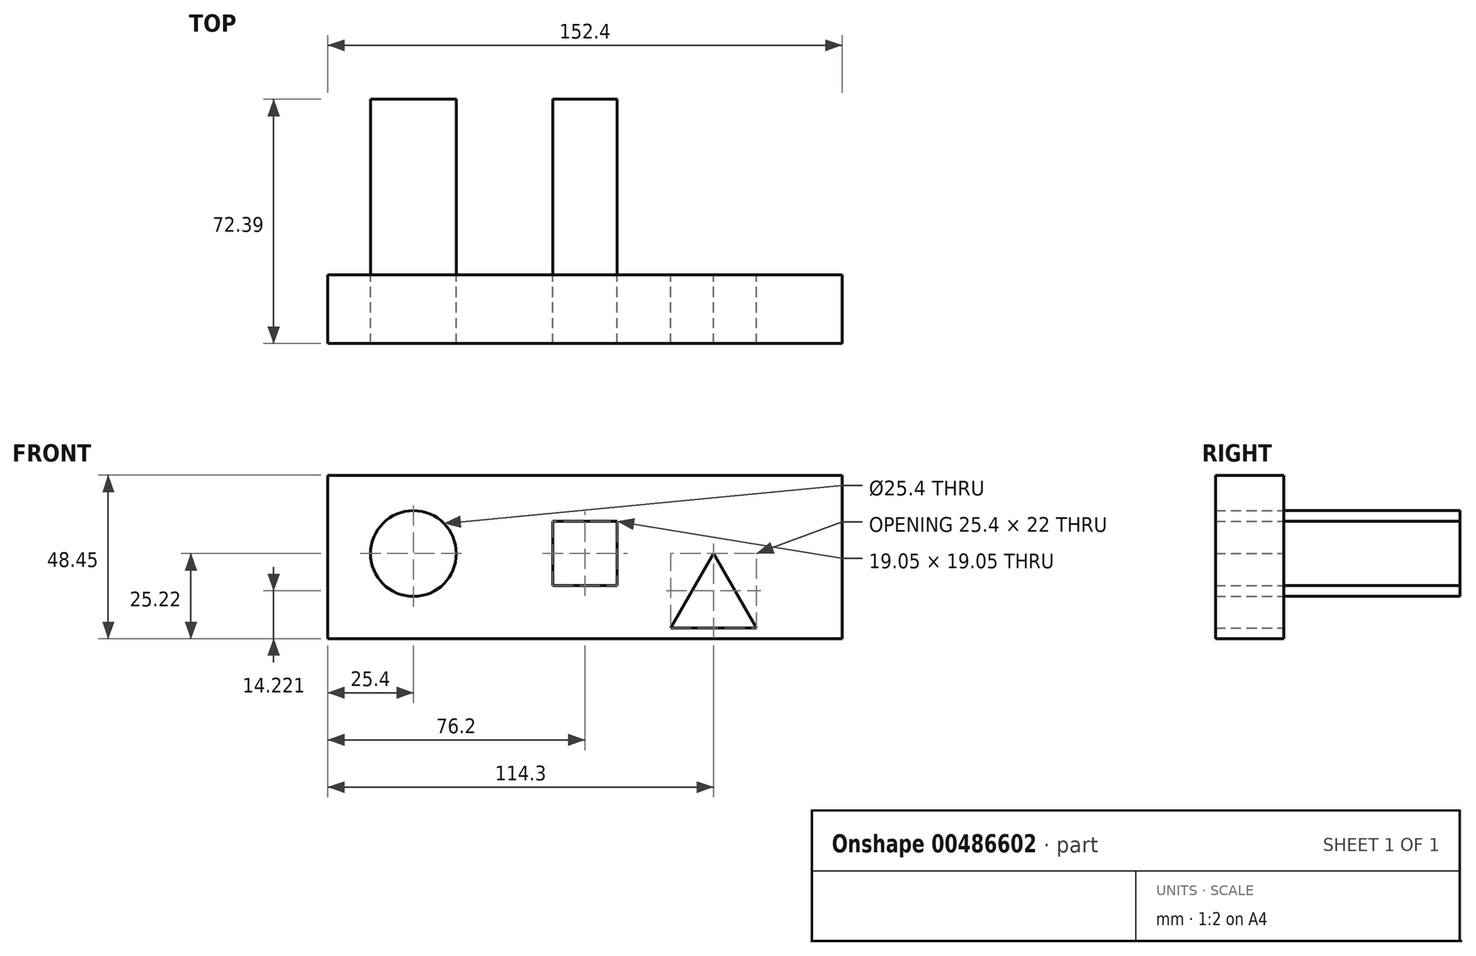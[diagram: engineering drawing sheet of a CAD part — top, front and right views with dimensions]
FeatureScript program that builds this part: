
annotation { "Feature Type Name" : "Feature", "Feature Type Description" : "" }
export const myFeature = defineFeature(function(context is Context, id is Id, definition is map)
    precondition{}
    {
        {
            var Q0;
            Q0=qCreatedBy(makeId("Front.planeOp"),FACE);
            var sketch = newSketch(context, id + "F0", { "sketchPlane" : qUnion([Q0])});
            skPoint(sketch, "E0.middle", {"position": v(0, 0) * mm});
            skLineSegment(sketch, "E1", {"start": v(0, 0) * mm, "end": v(6.35, 0) * mm});
            skLineSegment(sketch, "E2", {"start": v(6.35, 0) * mm, "end": v(-6.35, -22) * mm});
            skLineSegment(sketch, "E3", {"start": v(6.35, 0) * mm, "end": v(19.05, -22) * mm});
            skLineSegment(sketch, "E4", {"start": v(19.05, -22) * mm, "end": v(-6.35, -22) * mm});
            skLineSegment(sketch, "E5", {"start": v(-31.75, 0) * mm, "end": v(0, 0) * mm});
            skLineSegment(sketch, "E6.bottom", {"start": v(-41.27, 9.53) * mm, "end": v(-22.22, 9.52) * mm});
            skLineSegment(sketch, "E6.top", {"start": v(-41.27, -9.53) * mm, "end": v(-22.23, -9.53) * mm});
            skLineSegment(sketch, "E6.left", {"start": v(-41.27, 9.53) * mm, "end": v(-41.28, -9.53) * mm});
            skLineSegment(sketch, "E6.right", {"start": v(-22.22, 9.52) * mm, "end": v(-22.23, -9.53) * mm});
            skPoint(sketch, "E6.middle", {"position": v(-31.75, 0) * mm});
            skLineSegment(sketch, "E7", {"start": v(-31.75, 0) * mm, "end": v(-82.55, 0) * mm});
            skCircle(sketch, "E8", {"center": v(-82.55, 0) * mm, "radius": 12.7 * mm});
            skLineSegment(sketch, "E9", {"start": v(0, 0) * mm, "end": v(44.45, 0) * mm});
            skPoint(sketch, "E9.endSnap0", {"position": v(3.18, 0) * mm});
            skLineSegment(sketch, "E10", {"start": v(44.45, 0) * mm, "end": v(44.45, -25.22) * mm});
            skLineSegment(sketch, "E11.bottom", {"start": v(44.45, -25.22) * mm, "end": v(-107.95, -25.22) * mm});
            skLineSegment(sketch, "E11.top", {"start": v(44.45, 23.23) * mm, "end": v(-107.95, 23.23) * mm});
            skLineSegment(sketch, "E11.left", {"start": v(44.45, -25.22) * mm, "end": v(44.45, 23.23) * mm});
            skLineSegment(sketch, "E11.right", {"start": v(-107.95, -25.22) * mm, "end": v(-107.95, 23.23) * mm});
            skSolve(sketch);
        }
        {
            var Q0;
            Q0 = qSketchRegion(id + "F0", true);
            extrude(context, id + "F1", {"entities" : qUnion([Q0]), "depth" : 20.32 * mm});
        }
        {
            var Q0;
            Q0=makeQuery(id+"F0.imprint","IMPRINT",FACE,{"disambiguationData":[TD([[makeQuery(id+"F0.imprint","IMPRINT",EDGE,{"derivedFrom":sQuery(id+"F0.wireOp",EDGE,"E8")}),1.0]])]});
            var Q1;
            {var subQ1=sQuery(id+"F0.wireOp",EDGE,"E6.top");Q1=makeQuery(id+"F0.imprint","IMPRINT",FACE,{"disambiguationData":[TD([[makeQuery(id+"F0.imprint","IMPRINT",EDGE,{"derivedFrom":subQ1}),1.0]])]});}
            var Q2;
            {var subQ1=sQuery(id+"F0.wireOp",EDGE,"E6.bottom");Q2=makeQuery(id+"F0.imprint","IMPRINT",FACE,{"disambiguationData":[TD([[makeQuery(id+"F0.imprint","IMPRINT",EDGE,{"derivedFrom":subQ1}),-1.0]])]});}
            extrude(context, id + "F2", {"entities" : qUnion([Q0, Q1, Q2]), "oppositeDirection" : true, "depth" : 52.07 * mm});
        }
        {
            var Q0;
            Q0=makeQuery(id+"F0.imprint","IMPRINT",FACE,{"disambiguationData":[TD([[makeQuery(id+"F0.imprint","IMPRINT",EDGE,{"derivedFrom":sQuery(id+"F0.wireOp",EDGE,"E8")}),1.0]])]});
            var Q1;
            {var subQ1=sQuery(id+"F0.wireOp",EDGE,"E6.top");Q1=makeQuery(id+"F0.imprint","IMPRINT",FACE,{"disambiguationData":[TD([[makeQuery(id+"F0.imprint","IMPRINT",EDGE,{"derivedFrom":subQ1}),1.0]])]});}
            var Q2;
            {var subQ1=sQuery(id+"F0.wireOp",EDGE,"E6.bottom");Q2=makeQuery(id+"F0.imprint","IMPRINT",FACE,{"disambiguationData":[TD([[makeQuery(id+"F0.imprint","IMPRINT",EDGE,{"derivedFrom":subQ1}),-1.0]])]});}
            extrude(context, id + "F3", {"entities" : qUnion([Q0, Q1, Q2]), "depth" : 20.32 * mm});
        }
    });
